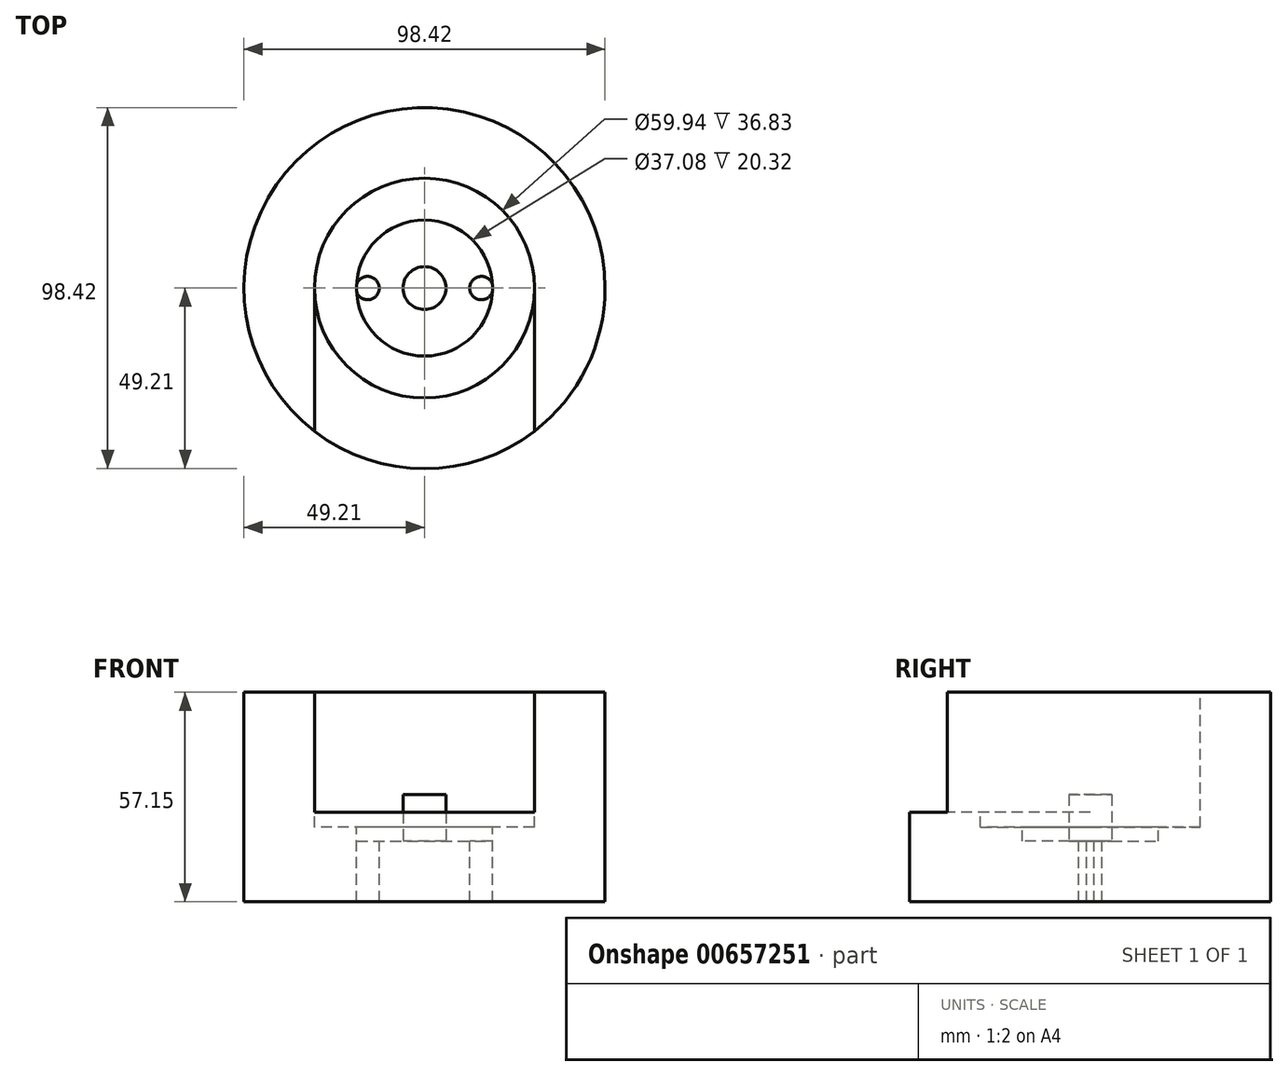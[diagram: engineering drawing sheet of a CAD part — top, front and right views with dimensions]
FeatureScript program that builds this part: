
annotation { "Feature Type Name" : "Feature", "Feature Type Description" : "" }
export const myFeature = defineFeature(function(context is Context, id is Id, definition is map)
    precondition{}
    {
        {
            var Q0;
            Q0=qCreatedBy(makeId("Top.planeOp"),FACE);
            var sketch = newSketch(context, id + "F0", { "sketchPlane" : qUnion([Q0])});
            skCircle(sketch, "E0", {"center": v(0, 0) * mm, "radius": 49.21 * mm});
            skSolve(sketch);
        }
        {
            var Q0;
            Q0 = qSketchRegion(id + "F0", true);
            extrude(context, id + "F1", {"entities" : qUnion([Q0]), "oppositeDirection" : true, "depth" : 57.15 * mm, "offsetDistance" : 25.4 * mm});
        }
        {
            var Q0;
            Q0=makeQuery(id+"F1.opExtrude","CAP_FACE",FACE,{"disambiguationData":[OSD([sQuery(id+"F0.wireOp",EDGE,"E0")])],"isStart":true});
            var sketch = newSketch(context, id + "F2", { "sketchPlane" : qUnion([Q0])});
            skCircle(sketch, "E1", {"center": v(0, 0) * mm, "radius": 18.54 * mm});
            skCircle(sketch, "E2", {"center": v(0, 0) * mm, "radius": 29.97 * mm});
            skLineSegment(sketch, "E3", {"start": v(-29.97, 0) * mm, "end": v(-29.97, -39.03) * mm});
            skLineSegment(sketch, "E4", {"start": v(29.97, 0) * mm, "end": v(29.97, -39.03) * mm});
            skLineSegment(sketch, "E5", {"start": v(-17.35, 46.05) * mm, "end": v(15.66, 46.65) * mm});
            skSolve(sketch);
        }
        {
            var Q0;
            Q0=makeQuery(id+"F2.imprint","IMPRINT",FACE,{"disambiguationData":[TD([[makeQuery(id+"F2.imprint","IMPRINT",EDGE,{"derivedFrom":sQuery(id+"F2.wireOp",EDGE,"E1")}),1.0]])]});
            extrude(context, id + "F3", {"entities" : qUnion([Q0]), "operationType" : NewBodyOperationType.REMOVE, "oppositeDirection" : true, "depth" : 40.64 * mm, "offsetDistance" : 25.4 * mm});
        }
        {
            var Q0;
            Q0=makeQuery(id+"F2.imprint","IMPRINT",FACE,{"disambiguationData":[TD([[makeQuery(id+"F2.imprint","IMPRINT",EDGE,{"derivedFrom":sQuery(id+"F2.wireOp",EDGE,"E1")}),-1.0]])]});
            extrude(context, id + "F4", {"entities" : qUnion([Q0]), "operationType" : NewBodyOperationType.REMOVE, "oppositeDirection" : true, "depth" : 36.83 * mm, "offsetDistance" : 25.4 * mm});
        }
        {
            var Q0;
            {var subQ0=sQuery(id+"F2.wireOp",EDGE,"E3");Q0=makeQuery(id+"F2.imprint","IMPRINT",FACE,{"disambiguationData":[TD([[makeQuery(id+"F2.imprint","IMPRINT",EDGE,{"derivedFrom":subQ0}),1.0]])]});}
            extrude(context, id + "F5", {"entities" : qUnion([Q0]), "operationType" : NewBodyOperationType.REMOVE, "oppositeDirection" : true, "depth" : 32.77 * mm, "offsetDistance" : 25.4 * mm});
        }
        {
            var Q0;
            Q0=makeQuery(id+"F3.boolean.opBoolean","COPY",FACE,{"derivedFrom":makeQuery(id+"F3.opExtrude","CAP_FACE",FACE,{"disambiguationData":[OSD([sQuery(id+"F2.wireOp",EDGE,"E1")])],"isStart":false})});
            var sketch = newSketch(context, id + "F6", { "sketchPlane" : qUnion([Q0])});
            skCircle(sketch, "E6", {"center": v(0, 0) * mm, "radius": 5.84 * mm});
            skSolve(sketch);
        }
        {
            var Q0;
            Q0=makeQuery(id+"F6.imprint","IMPRINT",FACE,{"disambiguationData":[TD([[makeQuery(id+"F6.imprint","IMPRINT",EDGE,{"derivedFrom":sQuery(id+"F6.wireOp",EDGE,"E6")}),1.0]])]});
            extrude(context, id + "F7", {"entities" : qUnion([Q0]), "operationType" : NewBodyOperationType.ADD, "depth" : 12.7 * mm, "offsetDistance" : 25.4 * mm});
        }
        {
            var Q0;
            Q0=makeQuery(id+"F3.boolean.opBoolean","COPY",FACE,{"derivedFrom":makeQuery(id+"F3.opExtrude","CAP_FACE",FACE,{"disambiguationData":[OSD([sQuery(id+"F2.wireOp",EDGE,"E1")])],"isStart":false})});
            var sketch = newSketch(context, id + "F8", { "sketchPlane" : qUnion([Q0])});
            skCircle(sketch, "E7", {"center": v(-15.5, 0) * mm, "radius": 3.18 * mm});
            skCircle(sketch, "E8", {"center": v(15.5, 0) * mm, "radius": 3.18 * mm});
            skSolve(sketch);
        }
        {
            var Q0;
            {var subQ0=sQuery(id+"F8.wireOp",EDGE,"E7");var subQ1=makeQuery(id+"F3.boolean.opBoolean","COPY",EDGE,{"derivedFrom":makeQuery(id+"F3.opExtrude","CAP_EDGE",EDGE,{"disambiguationData":[OSD([sQuery(id+"F2.wireOp",EDGE,"E1")])],"isStart":false})});var subQ2=makeQuery(id+"F8.imprint","INTERSECT",VERTEX,{"disambiguationData":[OD(0.0)],"derivedFrom":[subQ1,subQ0]});Q0=makeQuery(id+"F8.imprint","IMPRINT",FACE,{"disambiguationData":[TD([[makeQuery(id+"F8.imprint","IMPRINT",EDGE,{"disambiguationData":[TD([[subQ2,-1.0]])],"derivedFrom":subQ0}),1.0]])]});}
            var Q1;
            {var subQ0=sQuery(id+"F8.wireOp",EDGE,"E8");var subQ1=makeQuery(id+"F3.boolean.opBoolean","COPY",EDGE,{"derivedFrom":makeQuery(id+"F3.opExtrude","CAP_EDGE",EDGE,{"disambiguationData":[OSD([sQuery(id+"F2.wireOp",EDGE,"E1")])],"isStart":false})});var subQ2=makeQuery(id+"F8.imprint","INTERSECT",VERTEX,{"disambiguationData":[OD(0.0)],"derivedFrom":[subQ1,subQ0]});Q1=makeQuery(id+"F8.imprint","IMPRINT",FACE,{"disambiguationData":[TD([[makeQuery(id+"F8.imprint","IMPRINT",EDGE,{"disambiguationData":[TD([[subQ2,1.0]])],"derivedFrom":subQ0}),1.0]])]});}
            extrude(context, id + "F9", {"entities" : qUnion([Q0, Q1]), "operationType" : NewBodyOperationType.REMOVE, "endBound" : BoundingType.THROUGH_ALL, "oppositeDirection" : true, "depth" : 25.4 * mm, "offsetDistance" : 25.4 * mm});
        }
    });
